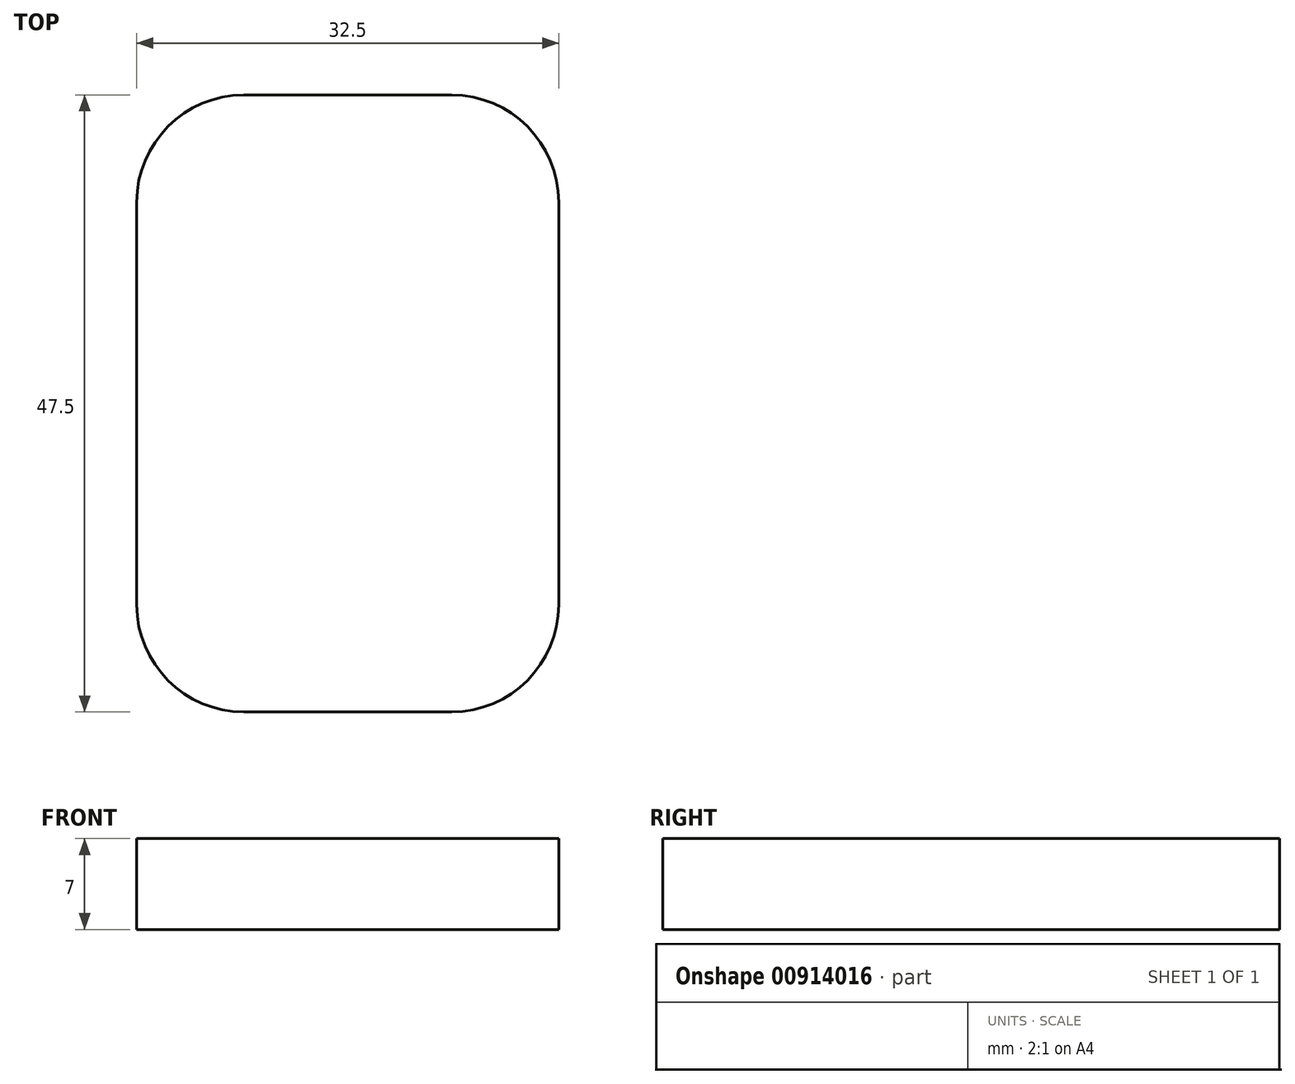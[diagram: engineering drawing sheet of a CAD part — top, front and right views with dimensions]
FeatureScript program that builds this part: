
annotation { "Feature Type Name" : "Feature", "Feature Type Description" : "" }
export const myFeature = defineFeature(function(context is Context, id is Id, definition is map)
    precondition{}
    {
        {
            var Q0;
            Q0=qCreatedBy(makeId("Top.planeOp"), FACE);
            var sketch = newSketch(context, id + "F0", { "sketchPlane" : qUnion([Q0])});
            skLineSegment(sketch, "E0.bottom", {"start": v(-8.01, 23.75) * mm, "end": v(7.99, 23.75) * mm});
            skLineSegment(sketch, "E0.top", {"start": v(-8.01, -23.75) * mm, "end": v(7.99, -23.75) * mm});
            skLineSegment(sketch, "E0.left", {"start": v(-16.26, 15.5) * mm, "end": v(-16.26, -15.5) * mm});
            skLineSegment(sketch, "E0.right", {"start": v(16.24, 15.5) * mm, "end": v(16.24, -15.5) * mm});
            skPoint(sketch, "E1.visualSharp", {"position": v(16.24, 23.75) * mm});
            skArc(sketch, "E1.filletArc", {"start": v(16.24, 15.5) * mm, "mid": v(13.82, 21.33) * mm, "end": v(7.99, 23.75) * mm});
            skPoint(sketch, "E2.visualSharp", {"position": v(16.24, -23.75) * mm});
            skArc(sketch, "E2.filletArc", {"start": v(7.99, -23.75) * mm, "mid": v(13.82, -21.33) * mm, "end": v(16.24, -15.5) * mm});
            skPoint(sketch, "E3.visualSharp", {"position": v(-16.26, -23.75) * mm});
            skArc(sketch, "E3.filletArc", {"start": v(-16.26, -15.5) * mm, "mid": v(-13.84, -21.33) * mm, "end": v(-8.01, -23.75) * mm});
            skPoint(sketch, "E4.visualSharp", {"position": v(-16.26, 23.75) * mm});
            skArc(sketch, "E4.filletArc", {"start": v(-8.01, 23.75) * mm, "mid": v(-13.84, 21.33) * mm, "end": v(-16.26, 15.5) * mm});
            skSolve(sketch);
        }
        {
            var Q0;
            Q0 = qSketchRegion(id + "F0", true);
            extrude(context, id + "F1", {"entities" : qUnion([Q0]), "domain" : OperationDomain.MODEL, "flatOperationType" : FlatOperationType.REMOVE, "depth" : 7 * mm, "offsetDistance" : 25 * mm});
        }
    });
